# Revit family: CBCONFTYP001
name_source: partatom
category: Furniture
units: mm (PartAtom-declared; Revit-internal decimal feet)

## family parameters
Always vertical = Yes
Cut with Voids When Loaded = No
OmniClass Number = 23.40.20.00
OmniClass Title = General Furniture and Specialties
Render Appearance Source = Family Geometry
Room Calculation Point = No
Shared = No
Work Plane-Based = No

## types (1)
- CBCONFTYP001
    Cost = 24735 $
    Default Elevation = 0 mm  [stored 0 ft]
    Description = 8 x Auburn Gray Conference Chair - Express, 2 x LB OTTOMAN 18"H X 24"W X 24"D W/FEET, 1 x CBX Buffet With Cabinet Doors 24D x 72W, 1 x Cbx Full Depth Floor Bookcase 18dx21hx72w, 1 x Cbx Table Rectangle 48D X 144W 2Mm 3 Sec 3 A-Base
    Exported From CET Designer = Yes
    Manufacturer = AIS
    Model = 7730
    Show CBCONFTYP001 = Yes
    VisibilityIndex = 0

note: [stored X ft] marks values corroborated as IEEE doubles in the binary element streams (Revit-internal decimal feet)

## geometry (parser evidence)
native form markers: Sweep x3
no freeform markers — native parametric forms only
